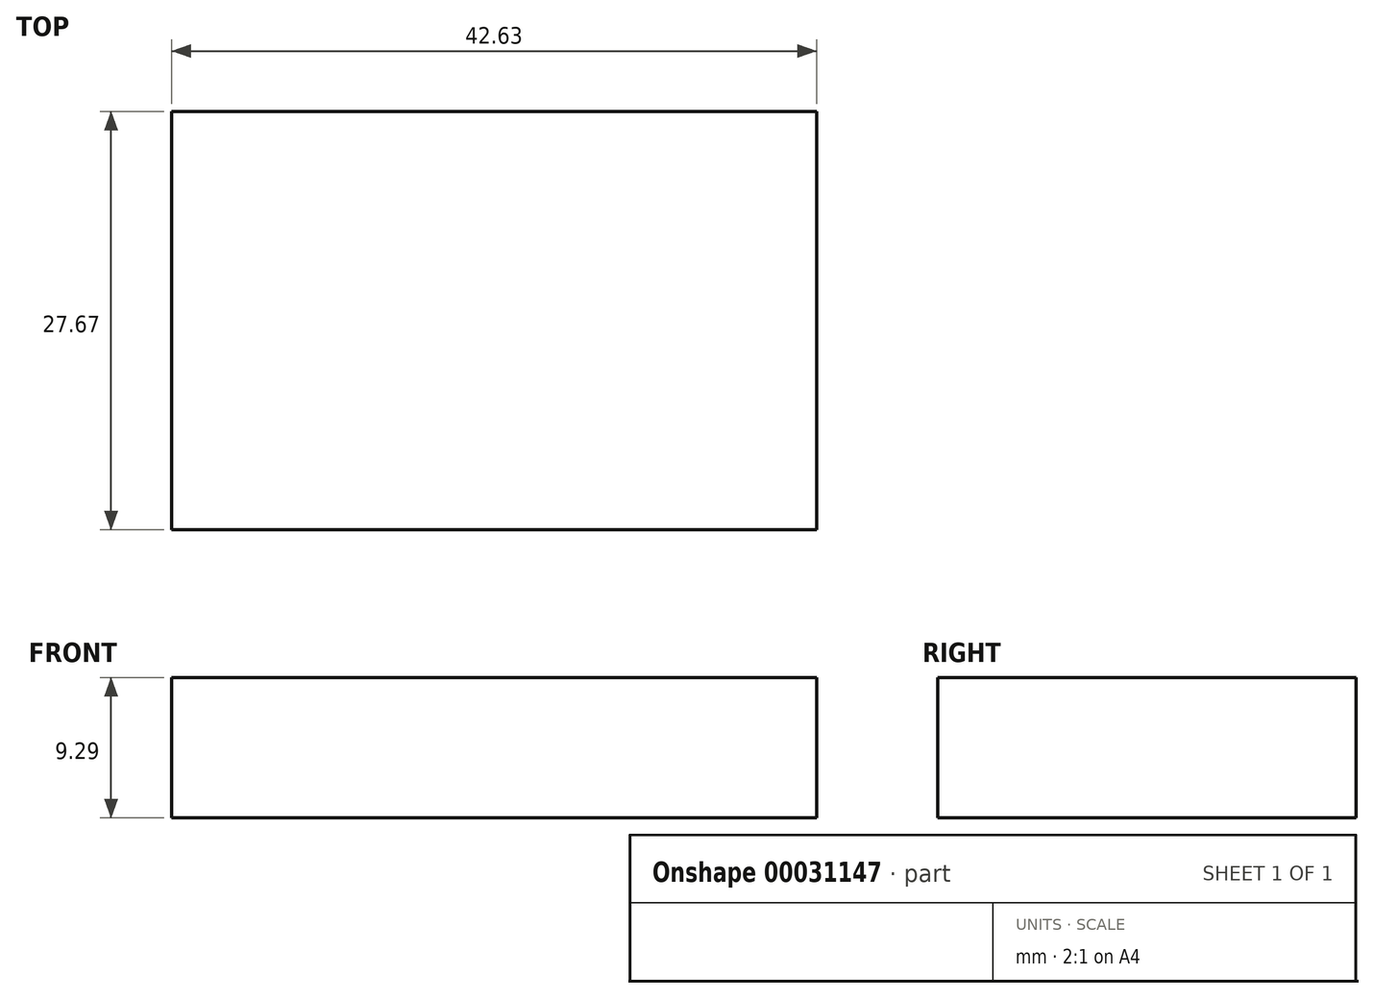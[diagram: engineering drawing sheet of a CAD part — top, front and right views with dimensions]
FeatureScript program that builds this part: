
annotation { "Feature Type Name" : "Feature", "Feature Type Description" : "" }
export const myFeature = defineFeature(function(context is Context, id is Id, definition is map)
    precondition{}
    {
        {
            var Q0;
            Q0=qCreatedBy(makeId("Top.planeOp"),FACE);
            var sketch = newSketch(context, id + "F0", { "sketchPlane" : qUnion([Q0])});
            skLineSegment(sketch, "E0.bottom", {"start": v(0, 0) * mm, "end": v(-42.63, 0) * mm});
            skLineSegment(sketch, "E0.top", {"start": v(0, 27.67) * mm, "end": v(-42.63, 27.67) * mm});
            skLineSegment(sketch, "E0.left", {"start": v(0, 0) * mm, "end": v(0, 27.67) * mm});
            skLineSegment(sketch, "E0.right", {"start": v(-42.63, 0) * mm, "end": v(-42.63, 27.67) * mm});
            skSolve(sketch);
        }
        {
            var Q0;
            Q0=makeQuery(id+"F0.imprint","IMPRINT",FACE,{"disambiguationData":[TD([[makeQuery(id+"F0.imprint","IMPRINT",EDGE,{"derivedFrom":sQuery(id+"F0.wireOp",EDGE,"E0.bottom")}),-1.0]])]});
            extrude(context, id + "F1", {"entities" : qUnion([Q0]), "depth" : 9.29 * mm});
        }
    });
